# Revit family: LEGRAND_NON INTERLOCKED SOCKETS_FLUSH MOUNTED_IP66_400
name_source: partatom
category: Installations électriques
revit_build: Autodesk Revit 2018 (Build: 20170223_1515(x64)
units: mm (PartAtom-declared; Revit-internal decimal feet)

## family parameters
Conserver l'orientation des annotations = Non
Cote de connecteur circulaire = Utiliser le diamètre
Couper avec des vides une fois chargée = Non
Hôte = Face
Partagée = Non
Point de calcul de pièce = Non
Type d'élément = Normal

## types (10) — shared parameters
Description = international standard socket for flush or surface mounting with accessory allows the connection of power devices
Elévation par défaut = 1000 mm
Fabricant = Legrand
Flush E or Surface mounting S = flush and surface mounting
General Conditions of Use = https://export.legrand.com
Maximum installation temperature = 40°C
Maximum use temperature = 100°C
Minimum installation temperature = -20°C
Minimum use temperature = -50°C
Standard IEC or NFC = IEC
Tension V = 400 V  50/60 Hz red
characteristic color = red
halogen free = Non
interlocking type = screw terminals
material of box = plastic
protection class IP = IP66/67-55
resistance to chocks IK = 09

## per-type parameters (varying)
| type | Dia bouchon | Modèle | Number of poles | Position of earth h | RAY BOUCHON | Ray | dIA | depth for flush mounting mm | depth mm | h1 | height mm | horizontal fixing distance mm | intensity A | vertical fixing distance mm | width mm |
| panel mounting socket Hypra   IP66/67-55   16 A   380/415 V   3P+E   plast | 79 mm | 051130 | 4 | 6 | 40 mm | 26 mm | 53 mm | 41 mm  [stored 0.134514 ft] | 89 mm  [stored 0.291995 ft] | 50 mm  [stored 0.164042 ft] | 84 mm | 60 mm | 16 A | 70 mm | 74 mm |
| panel mounting socket Hypra   IP66/67-55   16 A   380/415 V   3P+N+E   plast | 82 mm | 051131 | 6 | 6 | 41 mm  [stored 0.134514 ft] | 27 mm | 55 mm | 42 mm  [stored 0.137795 ft] | 92 mm | 50 mm  [stored 0.164042 ft] | 84 mm | 60 mm | 16 A | 70 mm | 80 mm |
| panel mounting socket single fixing center Hypra  IP66/67-55  16 A   380/415 V   3P+E   plast | 84 mm | 051150 | 4 | 6 | 42 mm  [stored 0.137795 ft] | 28 mm | 56 mm | 43 mm | 84 mm | 50 mm  [stored 0.164042 ft] | 84 mm | 70 mm | 16 A | 70 mm | 84 mm |
| panel mounting socket single fixing center Hypra  IP66/67-55  16 A  380/415 V   3P+N+E  plast | 84 mm | 051151 | 5 | 6 | 42 mm  [stored 0.137795 ft] | 28 mm | 56 mm | 43 mm | 84 mm | 50 mm  [stored 0.164042 ft] | 84 mm | 70 mm | 16 A | 70 mm | 84 mm |
| panel mounting socket single fixing center Hypra  IP66/67-55  32 A   380/415 V   3P+E   plast | 89 mm  [stored 0.291995 ft] | 053050 | 4 | 6 | 45 mm | 30 mm  [stored 0.0984252 ft] | 59 mm | 54 mm | 104 mm | 56 mm | 94 mm | 70 mm | 32 A | 70 mm | 84 mm |
| panel mounting socket single fixing center Hypra  IP66/67-55  32 A  380/415 V   3P+N+E  plast | 89 mm  [stored 0.291995 ft] | 053051 | 5 | 6 | 45 mm | 30 mm  [stored 0.0984252 ft] | 59 mm | 54 mm | 105 mm  [stored 0.344488 ft] | 56 mm | 94 mm | 70 mm | 32 A | 70 mm | 84 mm |
| panel mounting socket Hypra  IP66/67-55   63A   380 415 V   3P+E   plast | 106 mm | 059427 | 4 | 9 | 53 mm | 35 mm | 71 mm | 85 mm | 164 mm | 64 mm | 106 mm | 77 mm | 63 A | 85 mm | 106 mm |
| panel mounting socket Hypra  IP66/67-55   63A   380 415 V   3P+N+E   plast | 106 mm | 059428 | 4 | 9 | 53 mm | 35 mm | 71 mm | 85 mm | 164 mm | 64 mm | 106 mm | 77 mm | 63 A | 85 mm | 106 mm |
| panel mounting socket Hypra  IP66/67-55   125A   380 415 V   3P+E   plast | 146 mm  [stored 0.479003 ft] | 059512 | 4 | 6 | 73 mm  [stored 0.239501 ft] | 49 mm | 97 mm | 84 mm | 180 mm | 88 mm | 146 mm  [stored 0.479003 ft] | 124 mm | 125 A | 124 mm | 146 mm  [stored 0.479003 ft] |
| panel mounting socket Hypra  IP66/67-55   125A   380 415 V   3P+N+E   plast | 146 mm  [stored 0.479003 ft] | 059513 | 5 | 6 | 73 mm  [stored 0.239501 ft] | 49 mm | 97 mm | 84 mm | 180 mm | 88 mm | 146 mm  [stored 0.479003 ft] | 124 mm | 125 A | 124 mm | 146 mm  [stored 0.479003 ft] |

note: [stored X ft] marks values corroborated as IEEE doubles in the binary element streams (Revit-internal decimal feet)
